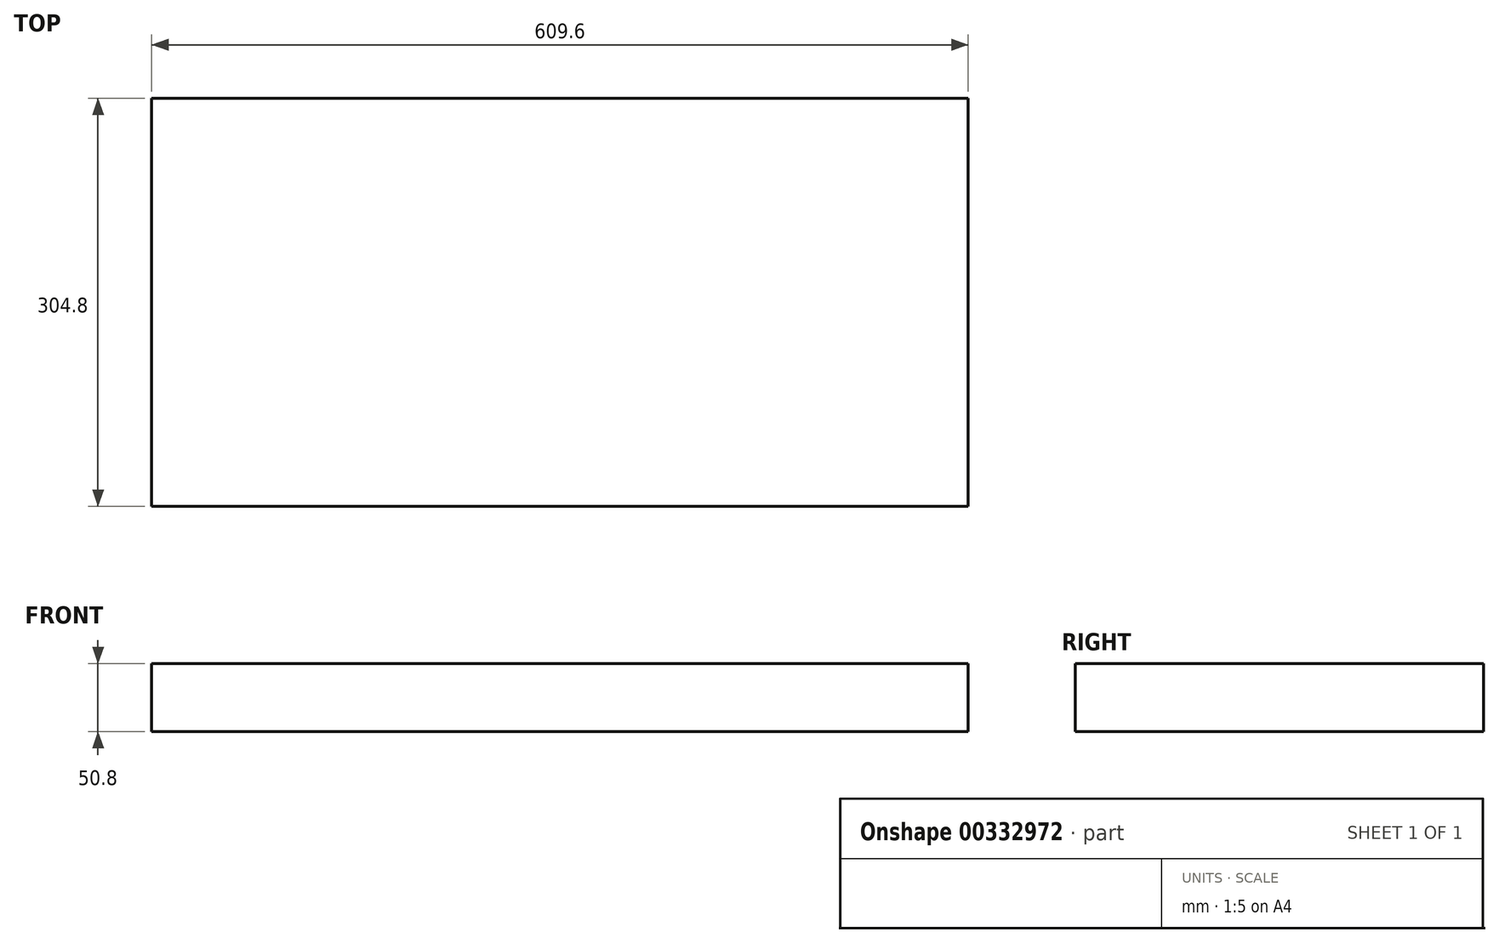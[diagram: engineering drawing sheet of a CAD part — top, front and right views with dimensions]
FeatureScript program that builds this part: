
annotation { "Feature Type Name" : "Feature", "Feature Type Description" : "" }
export const myFeature = defineFeature(function(context is Context, id is Id, definition is map)
    precondition{}
    {
        {
            var Q0;
            Q0=qCreatedBy(makeId("Top.planeOp"),FACE);
            var sketch = newSketch(context, id + "F0", { "sketchPlane" : qUnion([Q0])});
            skLineSegment(sketch, "E0.bottom", {"start": v(-354.63, 27.43) * mm, "end": v(254.97, 27.43) * mm});
            skLineSegment(sketch, "E0.top", {"start": v(-354.63, -277.37) * mm, "end": v(254.97, -277.37) * mm});
            skLineSegment(sketch, "E0.left", {"start": v(-354.63, 27.43) * mm, "end": v(-354.63, -277.37) * mm});
            skLineSegment(sketch, "E0.right", {"start": v(254.97, 27.43) * mm, "end": v(254.97, -277.37) * mm});
            skSolve(sketch);
        }
        {
            var Q0;
            Q0=makeQuery(id+"F0.imprint","IMPRINT",FACE,{"disambiguationData":[TD([[makeQuery(id+"F0.imprint","IMPRINT",EDGE,{"derivedFrom":sQuery(id+"F0.wireOp",EDGE,"E0.bottom")}),-1.0]])]});
            extrude(context, id + "F1", {"entities" : qUnion([Q0]), "depth" : 50.8 * mm});
        }
    });
